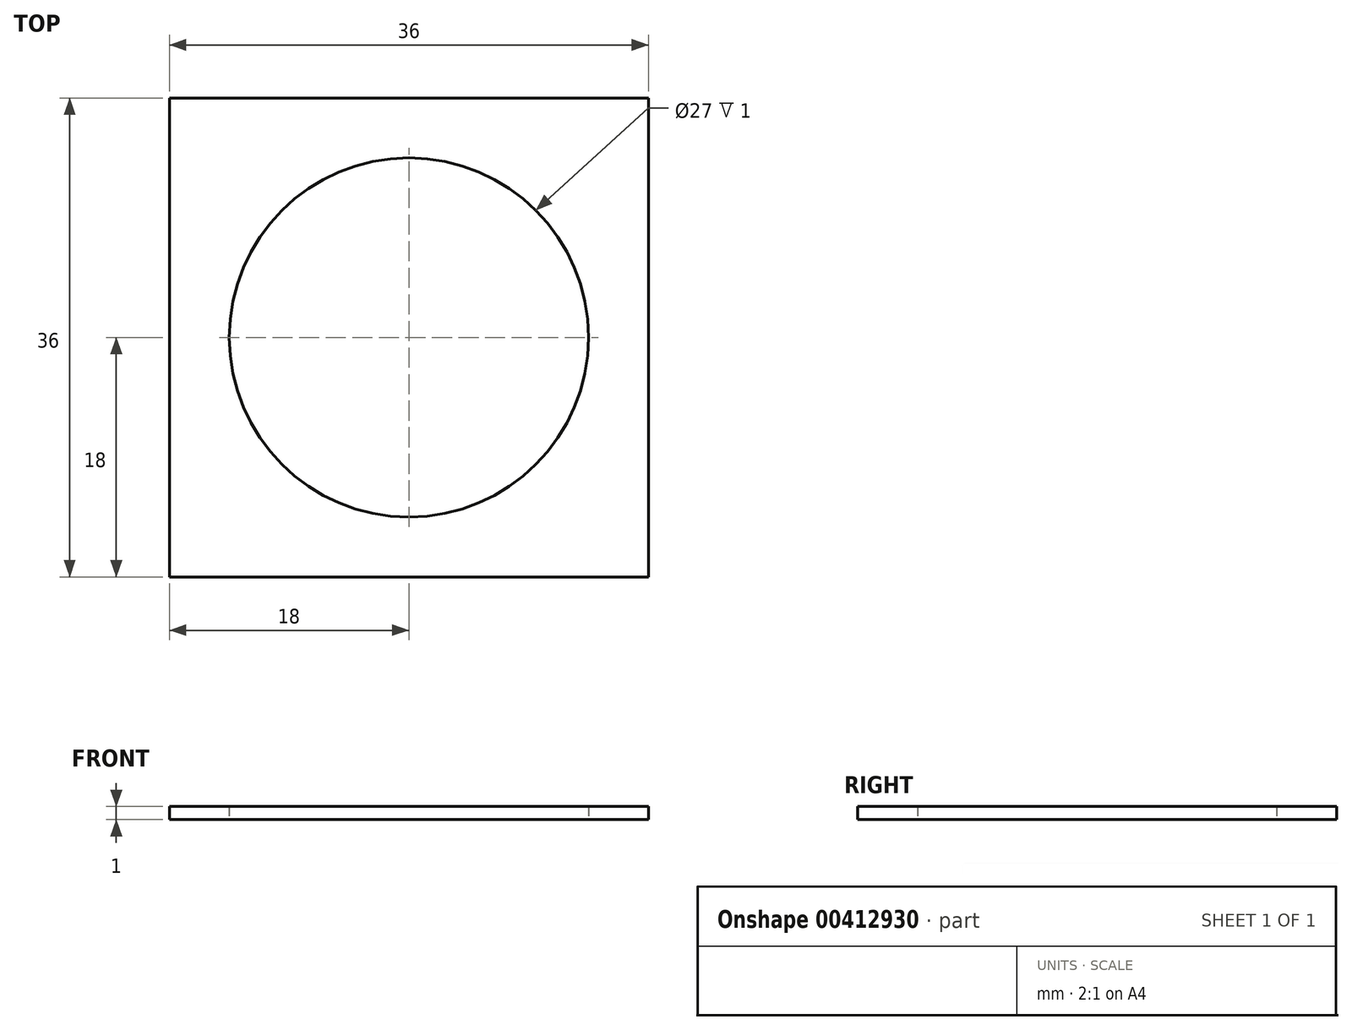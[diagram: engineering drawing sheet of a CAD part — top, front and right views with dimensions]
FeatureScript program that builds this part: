
annotation { "Feature Type Name" : "Feature", "Feature Type Description" : "" }
export const myFeature = defineFeature(function(context is Context, id is Id, definition is map)
    precondition{}
    {
        {
            var Q0;
            Q0=qCreatedBy(makeId("Top.planeOp"),FACE);
            var sketch = newSketch(context, id + "F0", { "sketchPlane" : qUnion([Q0])});
            skCircle(sketch, "E0", {"center": v(0, 0) * mm, "radius": 13.5 * mm});
            skLineSegment(sketch, "E1.bottom", {"start": v(18, 18) * mm, "end": v(-18, 18) * mm});
            skLineSegment(sketch, "E1.top", {"start": v(18, -18) * mm, "end": v(-18, -18) * mm});
            skLineSegment(sketch, "E1.left", {"start": v(18, 18) * mm, "end": v(18, -18) * mm});
            skLineSegment(sketch, "E1.right", {"start": v(-18, 18) * mm, "end": v(-18, -18) * mm});
            skSolve(sketch);
        }
        {
            var Q0;
            Q0=makeQuery(id+"F0.imprint","IMPRINT",FACE,{"disambiguationData":[TD([[makeQuery(id+"F0.imprint","IMPRINT",EDGE,{"derivedFrom":sQuery(id+"F0.wireOp",EDGE,"E0")}),-1.0]])]});
            extrude(context, id + "F1", {"entities" : qUnion([Q0]), "depth" : 1 * mm, "offsetDistance" : 25 * mm});
        }
    });
